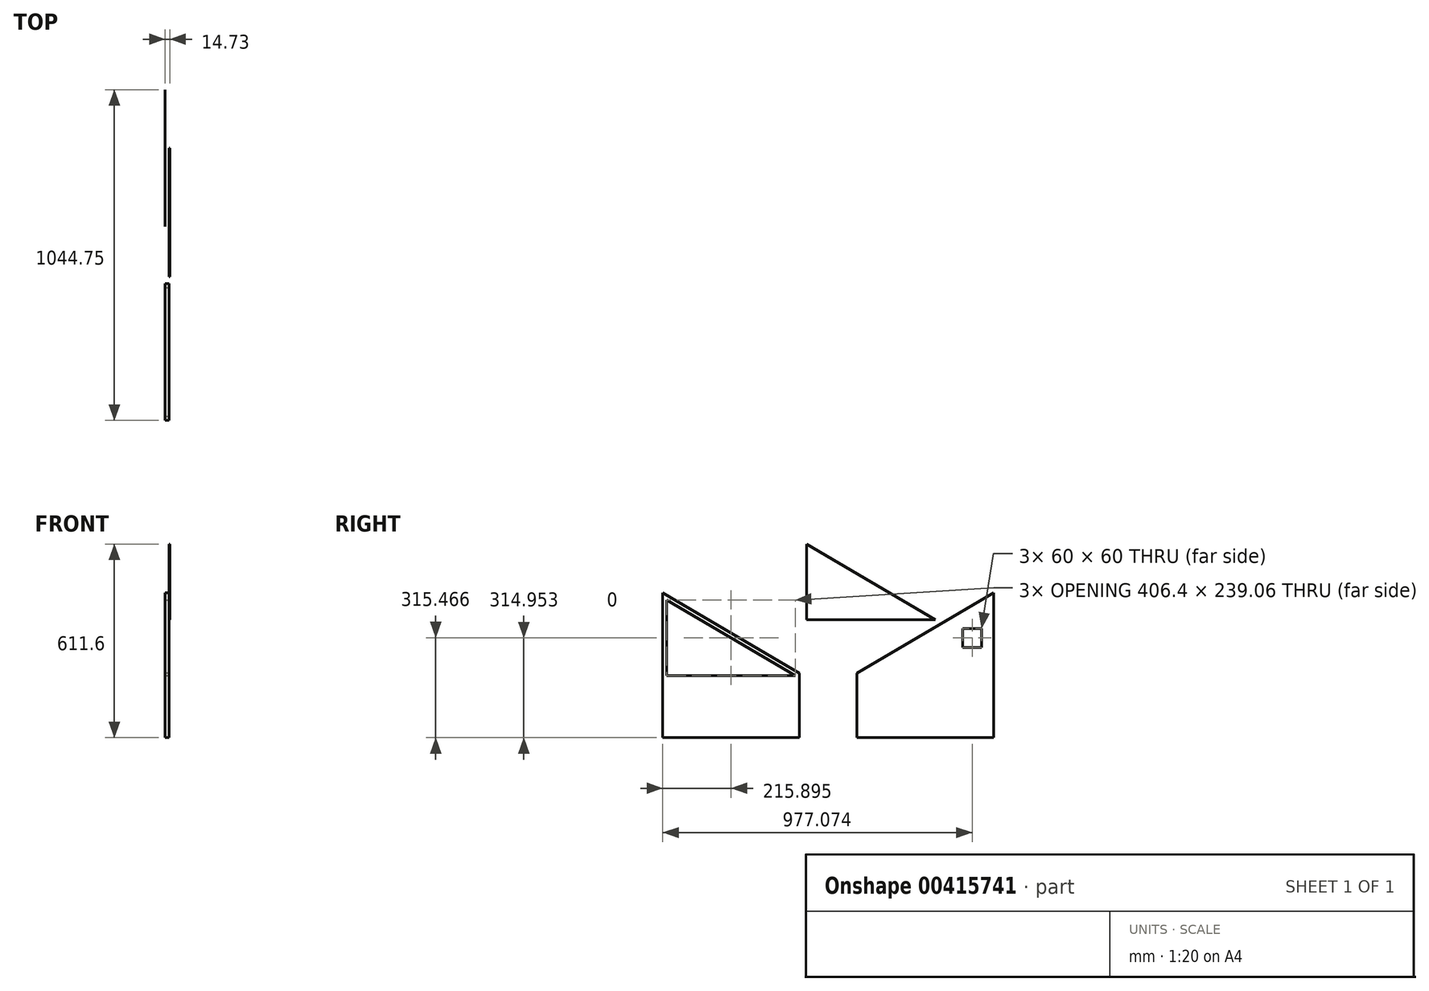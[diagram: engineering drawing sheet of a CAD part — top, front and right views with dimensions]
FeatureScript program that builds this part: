
annotation { "Feature Type Name" : "Feature", "Feature Type Description" : "" }
export const myFeature = defineFeature(function(context is Context, id is Id, definition is map)
    precondition{}
    {
        {
            var Q0;
            Q0=qCreatedBy(makeId("Right.planeOp"),FACE);
            var sketch = newSketch(context, id + "F0", { "sketchPlane" : qUnion([Q0])});
            skLineSegment(sketch, "E0", {"start": v(0, 0) * mm, "end": v(0, 203.2) * mm});
            skLineSegment(sketch, "E1", {"start": v(0, 203.2) * mm, "end": v(431.8, 457.2) * mm});
            skLineSegment(sketch, "E2", {"start": v(431.8, 457.2) * mm, "end": v(431.8, 0) * mm});
            skLineSegment(sketch, "E3", {"start": v(431.8, 0) * mm, "end": v(0, 0) * mm});
            skLineSegment(sketch, "E4", {"start": v(-181.15, 0) * mm, "end": v(-181.15, 203.2) * mm});
            skLineSegment(sketch, "E5", {"start": v(-181.15, 203.2) * mm, "end": v(-612.95, 457.2) * mm});
            skLineSegment(sketch, "E6", {"start": v(-612.95, 457.2) * mm, "end": v(-612.95, 0) * mm});
            skLineSegment(sketch, "E7", {"start": v(-612.95, 0) * mm, "end": v(-181.15, 0) * mm});
            skSolve(sketch);
        }
        {
            var Q0;
            Q0=makeQuery(id+"F0.imprint","IMPRINT",FACE,{"disambiguationData":[TD([[makeQuery(id+"F0.imprint","IMPRINT",EDGE,{"derivedFrom":sQuery(id+"F0.wireOp",EDGE,"E4")}),1.0]])]});
            extrude(context, id + "F1", {"entities" : qUnion([Q0]), "depth" : 12.7 * mm});
        }
        {
            var Q0;
            Q0=makeQuery(id+"F0.imprint","IMPRINT",FACE,{"disambiguationData":[TD([[makeQuery(id+"F0.imprint","IMPRINT",EDGE,{"derivedFrom":sQuery(id+"F0.wireOp",EDGE,"E0")}),-1.0]])]});
            extrude(context, id + "F2", {"entities" : qUnion([Q0]), "depth" : 1 / 50.8 * mm});
        }
        {
            var Q0;
            Q0=makeQuery(id+"F2.opExtrude","CAP_FACE",FACE,{"disambiguationData":[OSD([sQuery(id+"F0.wireOp",EDGE,"E0"),sQuery(id+"F0.wireOp",EDGE,"E1"),sQuery(id+"F0.wireOp",EDGE,"E2"),sQuery(id+"F0.wireOp",EDGE,"E3")])],"isStart":false});
            var sketch = newSketch(context, id + "F3", { "sketchPlane" : qUnion([Q0])});
            skLineSegment(sketch, "E8.bottom", {"start": v(394.12, 344.95) * mm, "end": v(334.12, 344.95) * mm});
            skLineSegment(sketch, "E8.top", {"start": v(394.12, 284.95) * mm, "end": v(334.12, 284.95) * mm});
            skLineSegment(sketch, "E8.left", {"start": v(394.12, 344.95) * mm, "end": v(394.12, 284.95) * mm});
            skLineSegment(sketch, "E8.right", {"start": v(334.12, 344.95) * mm, "end": v(334.12, 284.95) * mm});
            skSolve(sketch);
        }
        {
            var Q0;
            Q0=makeQuery(id+"F3.imprint","IMPRINT",FACE,{"disambiguationData":[TD([[makeQuery(id+"F3.imprint","IMPRINT",EDGE,{"derivedFrom":sQuery(id+"F3.wireOp",EDGE,"E8.bottom")}),1.0]])]});
            extrude(context, id + "F4", {"entities" : qUnion([Q0]), "operationType" : NewBodyOperationType.REMOVE, "oppositeDirection" : true, "depth" : 25.4 * mm});
        }
        {
            var Q0;
            Q0=makeQuery(id+"F1.opExtrude","CAP_FACE",FACE,{"disambiguationData":[OSD([sQuery(id+"F0.wireOp",EDGE,"E4"),sQuery(id+"F0.wireOp",EDGE,"E5"),sQuery(id+"F0.wireOp",EDGE,"E6"),sQuery(id+"F0.wireOp",EDGE,"E7")])],"isStart":false});
            var sketch = newSketch(context, id + "F5", { "sketchPlane" : qUnion([Q0])});
            skPoint(sketch, "E9", {"position": v(-600.25, 435) * mm});
            skPoint(sketch, "E10", {"position": v(-193.85, 195.94) * mm});
            skLineSegment(sketch, "E11", {"start": v(-600.25, 435) * mm, "end": v(-193.85, 195.94) * mm});
            skPoint(sketch, "E12", {"position": v(-600.25, 195.94) * mm});
            skLineSegment(sketch, "E13", {"start": v(-600.25, 435) * mm, "end": v(-600.25, 195.94) * mm});
            skLineSegment(sketch, "E14", {"start": v(-193.85, 195.94) * mm, "end": v(-600.25, 195.94) * mm});
            skPoint(sketch, "E15", {"position": v(-158.9, 372.54) * mm});
            skPoint(sketch, "E16", {"position": v(-158.9, 611.6) * mm});
            skPoint(sketch, "E17", {"position": v(247.5, 372.54) * mm});
            skLineSegment(sketch, "E18", {"start": v(-158.9, 611.6) * mm, "end": v(-158.9, 372.54) * mm});
            skLineSegment(sketch, "E19", {"start": v(247.5, 372.54) * mm, "end": v(-158.9, 372.54) * mm});
            skLineSegment(sketch, "E20", {"start": v(-158.9, 611.6) * mm, "end": v(247.5, 372.54) * mm});
            skPoint(sketch, "E21", {"position": v(-600.25, 170.54) * mm});
            skPoint(sketch, "E22", {"position": v(-193.85, 170.54) * mm});
            skPoint(sketch, "E23", {"position": v(-193.85, 12.7) * mm});
            skPoint(sketch, "E24", {"position": v(-600.25, 12.7) * mm});
            skLineSegment(sketch, "E25", {"start": v(-600.25, 170.54) * mm, "end": v(-193.85, 170.54) * mm});
            skLineSegment(sketch, "E26", {"start": v(-193.85, 12.7) * mm, "end": v(-193.85, 170.54) * mm});
            skLineSegment(sketch, "E27", {"start": v(-600.25, 12.7) * mm, "end": v(-193.85, 12.7) * mm});
            skLineSegment(sketch, "E28", {"start": v(-600.25, 170.54) * mm, "end": v(-600.25, 12.7) * mm});
            skSolve(sketch);
        }
        {
            var Q0;
            Q0=makeQuery(id+"F5.imprint","IMPRINT",FACE,{"disambiguationData":[TD([[makeQuery(id+"F5.imprint","IMPRINT",EDGE,{"derivedFrom":sQuery(id+"F5.wireOp",EDGE,"E18")}),1.0]])]});
            extrude(context, id + "F6", {"entities" : qUnion([Q0]), "depth" : 2.03 * mm});
        }
        {
            var Q0;
            Q0=makeQuery(id+"F5.imprint","IMPRINT",FACE,{"disambiguationData":[TD([[makeQuery(id+"F5.imprint","IMPRINT",EDGE,{"derivedFrom":sQuery(id+"F5.wireOp",EDGE,"E11")}),-1.0]])]});
            extrude(context, id + "F7", {"entities" : qUnion([Q0]), "operationType" : NewBodyOperationType.REMOVE, "oppositeDirection" : true, "depth" : 25.4 * mm});
        }
    });
